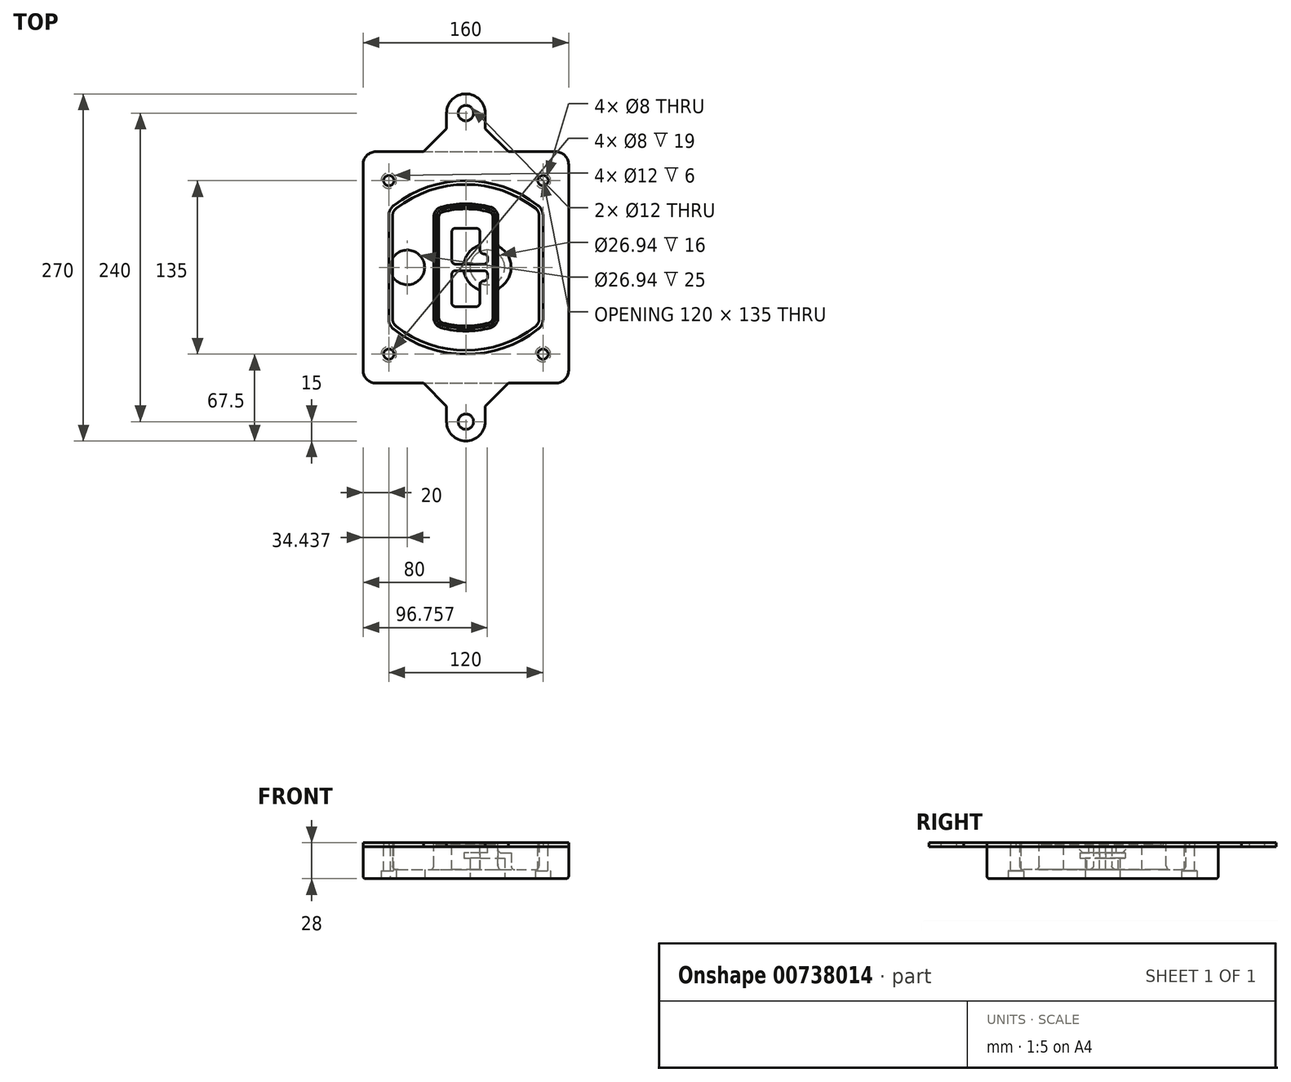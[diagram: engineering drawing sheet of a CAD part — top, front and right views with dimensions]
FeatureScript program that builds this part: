
annotation { "Feature Type Name" : "Feature", "Feature Type Description" : "" }
export const myFeature = defineFeature(function(context is Context, id is Id, definition is map)
    precondition{}
    {
        {
            var Q0;
            Q0=qCreatedBy(makeId("Top.planeOp"),FACE);
            var sketch = newSketch(context, id + "F0", { "sketchPlane" : qUnion([Q0])});
            skPoint(sketch, "E0.rect.middle", {"position": v(0, 0) * mm});
            skLineSegment(sketch, "E1.bottom", {"start": v(-70, -90) * mm, "end": v(70, -90) * mm});
            skLineSegment(sketch, "E1.top", {"start": v(-70, 90) * mm, "end": v(70, 90) * mm});
            skLineSegment(sketch, "E1.left", {"start": v(-80, -80) * mm, "end": v(-80, 80) * mm});
            skLineSegment(sketch, "E1.right", {"start": v(80, -80) * mm, "end": v(80, 80) * mm});
            skLineSegment(sketch, "E2", {"start": v(-80, 90) * mm, "end": v(80, -90) * mm, "construction": true});
            skLineSegment(sketch, "E3", {"start": v(80, 90) * mm, "end": v(-80, -90) * mm, "construction": true});
            skCircle(sketch, "E4", {"center": v(-60, 67.5) * mm, "radius": 4 * mm});
            skCircle(sketch, "E5", {"center": v(60, 67.5) * mm, "radius": 4 * mm});
            skCircle(sketch, "E6", {"center": v(60, -67.5) * mm, "radius": 4 * mm});
            skCircle(sketch, "E7", {"center": v(-60, -67.5) * mm, "radius": 4 * mm});
            skLineSegment(sketch, "E8", {"start": v(-60, 67.5) * mm, "end": v(60, 67.5) * mm, "construction": true});
            skLineSegment(sketch, "E9", {"start": v(60, 67.5) * mm, "end": v(60, -67.5) * mm, "construction": true});
            skLineSegment(sketch, "E10", {"start": v(60, -67.5) * mm, "end": v(-60, -67.5) * mm, "construction": true});
            skLineSegment(sketch, "E11", {"start": v(-60, -67.5) * mm, "end": v(-60, 67.5) * mm, "construction": true});
            skLineSegment(sketch, "E12", {"start": v(-60, 40.3) * mm, "end": v(-60, -40.3) * mm});
            skLineSegment(sketch, "E13", {"start": v(60, 40.3) * mm, "end": v(60, -40.3) * mm});
            skArc(sketch, "E14", {"start": v(56.15, 48.18) * mm, "mid": v(0, 67.5) * mm, "end": v(-56.15, 48.18) * mm});
            skArc(sketch, "E15", {"start": v(-56.15, -48.18) * mm, "mid": v(0, -67.5) * mm, "end": v(56.15, -48.18) * mm});
            skLineSegment(sketch, "E16", {"start": v(-60, 0) * mm, "end": v(60, 0) * mm, "construction": true});
            skPoint(sketch, "E17.visualSharp", {"position": v(-60, -45) * mm});
            skArc(sketch, "E17.filletArc", {"start": v(-60, -40.3) * mm, "mid": v(-58.99, -44.68) * mm, "end": v(-56.15, -48.18) * mm});
            skPoint(sketch, "E18.visualSharp", {"position": v(-60, 45) * mm});
            skArc(sketch, "E18.filletArc", {"start": v(-56.15, 48.18) * mm, "mid": v(-58.99, 44.68) * mm, "end": v(-60, 40.3) * mm});
            skPoint(sketch, "E19.visualSharp", {"position": v(60, 45) * mm});
            skArc(sketch, "E19.filletArc", {"start": v(60, 40.3) * mm, "mid": v(58.99, 44.68) * mm, "end": v(56.15, 48.18) * mm});
            skPoint(sketch, "E20.visualSharp", {"position": v(60, -45) * mm});
            skArc(sketch, "E20.filletArc", {"start": v(56.15, -48.18) * mm, "mid": v(58.99, -44.68) * mm, "end": v(60, -40.3) * mm});
            skPoint(sketch, "E21.visualSharp", {"position": v(-80, 90) * mm});
            skArc(sketch, "E21.filletArc", {"start": v(-70, 90) * mm, "mid": v(-77.07, 87.07) * mm, "end": v(-80, 80) * mm});
            skPoint(sketch, "E22.visualSharp", {"position": v(80, 90) * mm});
            skArc(sketch, "E22.filletArc", {"start": v(80, 80) * mm, "mid": v(77.07, 87.07) * mm, "end": v(70, 90) * mm});
            skPoint(sketch, "E23.visualSharp", {"position": v(80, -90) * mm});
            skArc(sketch, "E23.filletArc", {"start": v(70, -90) * mm, "mid": v(77.07, -87.07) * mm, "end": v(80, -80) * mm});
            skPoint(sketch, "E24.visualSharp", {"position": v(-80, -90) * mm});
            skArc(sketch, "E24.filletArc", {"start": v(-80, -80) * mm, "mid": v(-77.07, -87.07) * mm, "end": v(-70, -90) * mm});
            skArc(sketch, "E25.0", {"start": v(57, 40.3) * mm, "mid": v(56.3, 43.36) * mm, "end": v(54.3, 45.81) * mm});
            skLineSegment(sketch, "E25.1", {"start": v(57, 40.3) * mm, "end": v(57, -40.3) * mm});
            skArc(sketch, "E25.2", {"start": v(54.3, -45.81) * mm, "mid": v(56.3, -43.36) * mm, "end": v(57, -40.3) * mm});
            skArc(sketch, "E25.3", {"start": v(-54.3, -45.81) * mm, "mid": v(0, -64.5) * mm, "end": v(54.3, -45.81) * mm});
            skArc(sketch, "E25.4", {"start": v(-57, -40.3) * mm, "mid": v(-56.3, -43.36) * mm, "end": v(-54.3, -45.81) * mm});
            skArc(sketch, "E25.5", {"start": v(54.3, 45.81) * mm, "mid": v(0, 64.5) * mm, "end": v(-54.3, 45.81) * mm});
            skLineSegment(sketch, "E25.6", {"start": v(-57, 40.3) * mm, "end": v(-57, -40.3) * mm});
            skArc(sketch, "E25.7", {"start": v(-54.3, 45.81) * mm, "mid": v(-56.3, 43.36) * mm, "end": v(-57, 40.3) * mm});
            skArc(sketch, "E26.0", {"start": v(-58.62, 51.33) * mm, "mid": v(-62.58, 46.43) * mm, "end": v(-64, 40.3) * mm});
            skArc(sketch, "E26.1", {"start": v(58.62, 51.33) * mm, "mid": v(0, 71.5) * mm, "end": v(-58.62, 51.33) * mm});
            skArc(sketch, "E26.2", {"start": v(64, 40.3) * mm, "mid": v(62.58, 46.43) * mm, "end": v(58.62, 51.33) * mm});
            skLineSegment(sketch, "E26.3", {"start": v(64, 40.3) * mm, "end": v(64, -40.3) * mm});
            skArc(sketch, "E26.4", {"start": v(58.62, -51.33) * mm, "mid": v(62.58, -46.43) * mm, "end": v(64, -40.3) * mm});
            skLineSegment(sketch, "E26.5", {"start": v(-64, 40.3) * mm, "end": v(-64, -40.3) * mm});
            skArc(sketch, "E26.6", {"start": v(-58.62, -51.33) * mm, "mid": v(0, -71.5) * mm, "end": v(58.62, -51.33) * mm});
            skArc(sketch, "E26.7", {"start": v(-64, -40.3) * mm, "mid": v(-62.58, -46.43) * mm, "end": v(-58.62, -51.33) * mm});
            skSolve(sketch);
        }
        {
            var Q0;
            Q0=makeQuery(id+"F0.imprint","IMPRINT",FACE,{"disambiguationData":[TD([[makeQuery(id+"F0.imprint","IMPRINT",EDGE,{"derivedFrom":sQuery(id+"F0.wireOp",EDGE,"E1.bottom")}),1.0]])]});
            var Q1;
            Q1=makeQuery(id+"F0.imprint","IMPRINT",FACE,{"disambiguationData":[TD([[makeQuery(id+"F0.imprint","IMPRINT",EDGE,{"derivedFrom":sQuery(id+"F0.wireOp",EDGE,"E12")}),1.0]])]});
            var Q2;
            Q2=makeQuery(id+"F0.imprint","IMPRINT",FACE,{"disambiguationData":[TD([[makeQuery(id+"F0.imprint","IMPRINT",EDGE,{"derivedFrom":sQuery(id+"F0.wireOp",EDGE,"E25.0")}),1.0]])]});
            var Q3;
            Q3=makeQuery(id+"F0.imprint","IMPRINT",FACE,{"disambiguationData":[TD([[makeQuery(id+"F0.imprint","IMPRINT",EDGE,{"derivedFrom":sQuery(id+"F0.wireOp",EDGE,"E12")}),-1.0]])]});
            extrude(context, id + "F1", {"entities" : qUnion([Q0, Q1, Q2, Q3]), "oppositeDirection" : true, "depth" : 25 * mm});
        }
        {
            var Q0;
            Q0=makeQuery(id+"F0.imprint","IMPRINT",FACE,{"disambiguationData":[TD([[makeQuery(id+"F0.imprint","IMPRINT",EDGE,{"derivedFrom":sQuery(id+"F0.wireOp",EDGE,"E12")}),1.0]])]});
            extrude(context, id + "F2", {"entities" : qUnion([Q0]), "operationType" : NewBodyOperationType.ADD, "depth" : 3 * mm});
        }
        {
            var Q0;
            Q0=makeQuery(id+"F0.imprint","IMPRINT",FACE,{"disambiguationData":[TD([[makeQuery(id+"F0.imprint","IMPRINT",EDGE,{"derivedFrom":sQuery(id+"F0.wireOp",EDGE,"E25.0")}),1.0]])]});
            extrude(context, id + "F3", {"entities" : qUnion([Q0]), "operationType" : NewBodyOperationType.REMOVE, "oppositeDirection" : true, "depth" : 18 * mm});
        }
        {
            var Q0;
            Q0=makeQuery(id+"F2.opExtrude","CAP_FACE",FACE,{"disambiguationData":[OSD([sQuery(id+"F0.wireOp",EDGE,"E12"),sQuery(id+"F0.wireOp",EDGE,"E13"),sQuery(id+"F0.wireOp",EDGE,"E14"),sQuery(id+"F0.wireOp",EDGE,"E15"),sQuery(id+"F0.wireOp",EDGE,"E17.filletArc"),sQuery(id+"F0.wireOp",EDGE,"E18.filletArc"),sQuery(id+"F0.wireOp",EDGE,"E19.filletArc"),sQuery(id+"F0.wireOp",EDGE,"E20.filletArc"),sQuery(id+"F0.wireOp",EDGE,"E25.0"),sQuery(id+"F0.wireOp",EDGE,"E25.1"),sQuery(id+"F0.wireOp",EDGE,"E25.2"),sQuery(id+"F0.wireOp",EDGE,"E25.3"),sQuery(id+"F0.wireOp",EDGE,"E25.4"),sQuery(id+"F0.wireOp",EDGE,"E25.5"),sQuery(id+"F0.wireOp",EDGE,"E25.6"),sQuery(id+"F0.wireOp",EDGE,"E25.7")])],"isStart":false});
            var sketch = newSketch(context, id + "F4", { "sketchPlane" : qUnion([Q0])});
            skArc(sketch, "E27.0", {"start": v(-19.08, -46.97) * mm, "mid": v(0, -49.5) * mm, "end": v(19.08, -46.97) * mm});
            skArc(sketch, "E28.0", {"start": v(19.08, 46.97) * mm, "mid": v(0, 49.5) * mm, "end": v(-19.08, 46.97) * mm});
            skLineSegment(sketch, "E29", {"start": v(-25, 39.25) * mm, "end": v(-25, -39.25) * mm});
            skLineSegment(sketch, "E30", {"start": v(25, 39.25) * mm, "end": v(25, -39.25) * mm});
            skLineSegment(sketch, "E31", {"start": v(-25, 45.1) * mm, "end": v(25, 45.1) * mm, "construction": true});
            skLineSegment(sketch, "E32", {"start": v(-25, -45.1) * mm, "end": v(25, -45.1) * mm, "construction": true});
            skPoint(sketch, "E33.visualSharp", {"position": v(-25, 45.1) * mm});
            skArc(sketch, "E33.filletArc", {"start": v(-19.08, 46.97) * mm, "mid": v(-23.35, 44.11) * mm, "end": v(-25, 39.25) * mm});
            skPoint(sketch, "E34.visualSharp", {"position": v(25, 45.1) * mm});
            skArc(sketch, "E34.filletArc", {"start": v(25, 39.25) * mm, "mid": v(23.35, 44.11) * mm, "end": v(19.08, 46.97) * mm});
            skPoint(sketch, "E35.visualSharp", {"position": v(25, -45.1) * mm});
            skArc(sketch, "E35.filletArc", {"start": v(19.08, -46.97) * mm, "mid": v(23.35, -44.11) * mm, "end": v(25, -39.25) * mm});
            skPoint(sketch, "E36.visualSharp", {"position": v(-25, -45.1) * mm});
            skArc(sketch, "E36.filletArc", {"start": v(-25, -39.25) * mm, "mid": v(-23.35, -44.11) * mm, "end": v(-19.08, -46.97) * mm});
            skArc(sketch, "E37.0", {"start": v(54.3, 45.81) * mm, "mid": v(0, 64.5) * mm, "end": v(-54.3, 45.81) * mm});
            skArc(sketch, "E37.1", {"start": v(-54.3, 45.81) * mm, "mid": v(-56.3, 43.36) * mm, "end": v(-57, 40.3) * mm});
            skLineSegment(sketch, "E37.2", {"start": v(-57, 40.3) * mm, "end": v(-57, -40.3) * mm});
            skArc(sketch, "E37.3", {"start": v(-57, -40.3) * mm, "mid": v(-56.3, -43.36) * mm, "end": v(-54.3, -45.81) * mm});
            skArc(sketch, "E37.4", {"start": v(-54.3, -45.81) * mm, "mid": v(0, -64.5) * mm, "end": v(54.3, -45.81) * mm});
            skArc(sketch, "E37.5", {"start": v(54.3, -45.81) * mm, "mid": v(56.3, -43.36) * mm, "end": v(57, -40.3) * mm});
            skLineSegment(sketch, "E37.6", {"start": v(57, 40.3) * mm, "end": v(57, -40.3) * mm});
            skArc(sketch, "E37.7", {"start": v(57, 40.3) * mm, "mid": v(56.3, 43.36) * mm, "end": v(54.3, 45.81) * mm});
            skLineSegment(sketch, "E38.0", {"start": v(23, 39.25) * mm, "end": v(23, -39.25) * mm});
            skArc(sketch, "E38.1", {"start": v(18.56, -45.04) * mm, "mid": v(21.76, -42.9) * mm, "end": v(23, -39.25) * mm});
            skArc(sketch, "E38.2", {"start": v(-18.56, -45.04) * mm, "mid": v(0, -47.5) * mm, "end": v(18.56, -45.04) * mm});
            skArc(sketch, "E38.3", {"start": v(-23, -39.25) * mm, "mid": v(-21.76, -42.9) * mm, "end": v(-18.56, -45.04) * mm});
            skLineSegment(sketch, "E38.4", {"start": v(-23, 39.25) * mm, "end": v(-23, -39.25) * mm});
            skArc(sketch, "E38.5", {"start": v(23, 39.25) * mm, "mid": v(21.76, 42.9) * mm, "end": v(18.56, 45.04) * mm});
            skArc(sketch, "E38.6", {"start": v(-18.56, 45.04) * mm, "mid": v(-21.76, 42.9) * mm, "end": v(-23, 39.25) * mm});
            skArc(sketch, "E38.7", {"start": v(18.56, 45.04) * mm, "mid": v(0, 47.5) * mm, "end": v(-18.56, 45.04) * mm});
            skArc(sketch, "E39.0", {"start": v(21, 39.25) * mm, "mid": v(20.18, 41.68) * mm, "end": v(18.04, 43.1) * mm});
            skLineSegment(sketch, "E39.1", {"start": v(21, 39.25) * mm, "end": v(21, -39.25) * mm});
            skArc(sketch, "E39.2", {"start": v(18.04, -43.1) * mm, "mid": v(20.18, -41.68) * mm, "end": v(21, -39.25) * mm});
            skArc(sketch, "E39.3", {"start": v(-18.04, -43.1) * mm, "mid": v(0, -45.5) * mm, "end": v(18.04, -43.1) * mm});
            skArc(sketch, "E39.4", {"start": v(-21, -39.25) * mm, "mid": v(-20.18, -41.68) * mm, "end": v(-18.04, -43.1) * mm});
            skArc(sketch, "E39.5", {"start": v(18.04, 43.1) * mm, "mid": v(0, 45.5) * mm, "end": v(-18.04, 43.1) * mm});
            skLineSegment(sketch, "E39.6", {"start": v(-21, 39.25) * mm, "end": v(-21, -39.25) * mm});
            skArc(sketch, "E39.7", {"start": v(-18.04, 43.1) * mm, "mid": v(-20.18, 41.68) * mm, "end": v(-21, 39.25) * mm});
            skLineSegment(sketch, "E40", {"start": v(-25, 0) * mm, "end": v(25, 0) * mm, "construction": true});
            skLineSegment(sketch, "E41", {"start": v(-11, 5.5) * mm, "end": v(-11, 27.5) * mm});
            skLineSegment(sketch, "E42", {"start": v(-8, 30.5) * mm, "end": v(8, 30.5) * mm});
            skLineSegment(sketch, "E43", {"start": v(11, 27.5) * mm, "end": v(11, 13.5) * mm});
            skLineSegment(sketch, "E44", {"start": v(14, 10.5) * mm, "end": v(14, 10.5) * mm});
            skLineSegment(sketch, "E45", {"start": v(17, 7.5) * mm, "end": v(17, 5.5) * mm});
            skLineSegment(sketch, "E46", {"start": v(14, 2.5) * mm, "end": v(-8, 2.5) * mm});
            skPoint(sketch, "E47.visualSharp", {"position": v(-11, 30.5) * mm});
            skArc(sketch, "E47.filletArc", {"start": v(-8, 30.5) * mm, "mid": v(-10.12, 29.62) * mm, "end": v(-11, 27.5) * mm});
            skPoint(sketch, "E48.visualSharp", {"position": v(11, 30.5) * mm});
            skArc(sketch, "E48.filletArc", {"start": v(11, 27.5) * mm, "mid": v(10.12, 29.62) * mm, "end": v(8, 30.5) * mm});
            skPoint(sketch, "E49.visualSharp", {"position": v(11, 10.5) * mm});
            skArc(sketch, "E49.filletArc", {"start": v(11, 13.5) * mm, "mid": v(11.88, 11.38) * mm, "end": v(14, 10.5) * mm});
            skPoint(sketch, "E50.visualSharp", {"position": v(17, 10.5) * mm});
            skArc(sketch, "E50.filletArc", {"start": v(17, 7.5) * mm, "mid": v(16.12, 9.62) * mm, "end": v(14, 10.5) * mm});
            skPoint(sketch, "E51.visualSharp", {"position": v(17, 2.5) * mm});
            skArc(sketch, "E51.filletArc", {"start": v(14, 2.5) * mm, "mid": v(16.12, 3.38) * mm, "end": v(17, 5.5) * mm});
            skPoint(sketch, "E52.visualSharp", {"position": v(-11, 2.5) * mm});
            skArc(sketch, "E52.filletArc", {"start": v(-11, 5.5) * mm, "mid": v(-10.12, 3.38) * mm, "end": v(-8, 2.5) * mm});
            skLineSegment(sketch, "E53.0.MirrorCS", {"start": v(14, -2.5) * mm, "end": v(-8, -2.5) * mm});
            skArc(sketch, "E54.0.MirrorCS", {"start": v(-11, -5.5) * mm, "mid": v(-10.12, -3.38) * mm, "end": v(-8, -2.5) * mm});
            skLineSegment(sketch, "E55.0.MirrorCS", {"start": v(-11, -5.5) * mm, "end": v(-11, -27.5) * mm});
            skArc(sketch, "E56.0.MirrorCS", {"start": v(-8, -30.5) * mm, "mid": v(-10.12, -29.62) * mm, "end": v(-11, -27.5) * mm});
            skLineSegment(sketch, "E57.0.MirrorCS", {"start": v(-8, -30.5) * mm, "end": v(8, -30.5) * mm});
            skArc(sketch, "E58.0.MirrorCS", {"start": v(11, -27.5) * mm, "mid": v(10.12, -29.62) * mm, "end": v(8, -30.5) * mm});
            skLineSegment(sketch, "E59.0.MirrorCS", {"start": v(11, -27.5) * mm, "end": v(11, -13.5) * mm});
            skArc(sketch, "E60.0.MirrorCS", {"start": v(11, -13.5) * mm, "mid": v(11.88, -11.38) * mm, "end": v(14, -10.5) * mm});
            skArc(sketch, "E61.0.MirrorCS", {"start": v(17, -7.5) * mm, "mid": v(16.12, -9.62) * mm, "end": v(14, -10.5) * mm});
            skLineSegment(sketch, "E62.0.MirrorCS", {"start": v(17, -7.5) * mm, "end": v(17, -5.5) * mm});
            skArc(sketch, "E63.0.MirrorCS", {"start": v(14, -2.5) * mm, "mid": v(16.12, -3.38) * mm, "end": v(17, -5.5) * mm});
            skSolve(sketch);
        }
        {
            var Q0;
            Q0=makeQuery(id+"F4.imprint","IMPRINT",FACE,{"disambiguationData":[TD([[makeQuery(id+"F4.imprint","IMPRINT",EDGE,{"derivedFrom":sQuery(id+"F4.wireOp",EDGE,"E27.0")}),1.0]])]});
            var Q1;
            Q1=makeQuery(id+"F4.imprint","IMPRINT",FACE,{"disambiguationData":[TD([[makeQuery(id+"F4.imprint","IMPRINT",EDGE,{"derivedFrom":sQuery(id+"F4.wireOp",EDGE,"E38.0")}),-1.0]])]});
            var Q2;
            Q2=makeQuery(id+"F4.imprint","IMPRINT",FACE,{"disambiguationData":[TD([[makeQuery(id+"F4.imprint","IMPRINT",EDGE,{"derivedFrom":sQuery(id+"F4.wireOp",EDGE,"E39.0")}),1.0]])]});
            extrude(context, id + "F5", {"entities" : qUnion([Q0, Q1, Q2]), "operationType" : NewBodyOperationType.ADD, "endBound" : BoundingType.UP_TO_NEXT, "oppositeDirection" : true, "depth" : 25 * mm});
        }
        {
            var Q0;
            Q0=makeQuery(id+"F4.imprint","IMPRINT",FACE,{"disambiguationData":[TD([[makeQuery(id+"F4.imprint","IMPRINT",EDGE,{"derivedFrom":sQuery(id+"F4.wireOp",EDGE,"E38.0")}),-1.0]])]});
            extrude(context, id + "F6", {"entities" : qUnion([Q0]), "operationType" : NewBodyOperationType.REMOVE, "oppositeDirection" : true, "depth" : 2 * mm});
        }
        {
            var Q0;
            Q0=makeQuery(id+"F1.opExtrude","CAP_FACE",FACE,{"disambiguationData":[OSD([sQuery(id+"F0.wireOp",EDGE,"E1.bottom"),sQuery(id+"F0.wireOp",EDGE,"E1.top"),sQuery(id+"F0.wireOp",EDGE,"E1.left"),sQuery(id+"F0.wireOp",EDGE,"E1.right"),sQuery(id+"F0.wireOp",EDGE,"E4"),sQuery(id+"F0.wireOp",EDGE,"E5"),sQuery(id+"F0.wireOp",EDGE,"E6"),sQuery(id+"F0.wireOp",EDGE,"E7"),sQuery(id+"F0.wireOp",EDGE,"E21.filletArc"),sQuery(id+"F0.wireOp",EDGE,"E22.filletArc"),sQuery(id+"F0.wireOp",EDGE,"E23.filletArc"),sQuery(id+"F0.wireOp",EDGE,"E24.filletArc")])],"isStart":false});
            var sketch = newSketch(context, id + "F7", { "sketchPlane" : qUnion([Q0])});
            skCircle(sketch, "E64", {"center": v(16.76, 0) * mm, "radius": 13.47 * mm});
            skCircle(sketch, "E65", {"center": v(-45.56, 0) * mm, "radius": 13.47 * mm});
            skLineSegment(sketch, "E66", {"start": v(80, 0) * mm, "end": v(-80, 0) * mm});
            skCircle(sketch, "E67", {"center": v(16.76, 0) * mm, "radius": 18.47 * mm});
            skCircle(sketch, "E68", {"center": v(60, -67.5) * mm, "radius": 6 * mm});
            skCircle(sketch, "E69", {"center": v(-60, -67.5) * mm, "radius": 6 * mm});
            skCircle(sketch, "E70", {"center": v(-60, 67.5) * mm, "radius": 6 * mm});
            skCircle(sketch, "E71", {"center": v(60, 67.5) * mm, "radius": 6 * mm});
            skSolve(sketch);
        }
        {
            var Q0;
            {var subQ1=sQuery(id+"F7.wireOp",EDGE,"E66");var subQ4=sQuery(id+"F7.wireOp",EDGE,"E64");var subQ6=makeQuery(id+"F7.imprint","INTERSECT",VERTEX,{"disambiguationData":[OD(0.0)],"derivedFrom":[subQ4,subQ1]});Q0=makeQuery(id+"F7.imprint","IMPRINT",FACE,{"disambiguationData":[TD([[makeQuery(id+"F7.imprint","IMPRINT",EDGE,{"disambiguationData":[TD([[subQ6,-1.0]])],"derivedFrom":subQ4}),-1.0]])]});}
            var Q1;
            {var subQ0=sQuery(id+"F7.wireOp",EDGE,"E66");var subQ1=sQuery(id+"F7.wireOp",EDGE,"E64");var subQ3=makeQuery(id+"F7.imprint","INTERSECT",VERTEX,{"disambiguationData":[OD(0.0)],"derivedFrom":[subQ1,subQ0]});Q1=makeQuery(id+"F7.imprint","IMPRINT",FACE,{"disambiguationData":[TD([[makeQuery(id+"F7.imprint","IMPRINT",EDGE,{"disambiguationData":[TD([[subQ3,-1.0]])],"derivedFrom":subQ1}),1.0]])]});}
            var Q2;
            {var subQ0=sQuery(id+"F7.wireOp",EDGE,"E66");var subQ1=sQuery(id+"F7.wireOp",EDGE,"E64");var subQ3=makeQuery(id+"F7.imprint","INTERSECT",VERTEX,{"disambiguationData":[OD(0.0)],"derivedFrom":[subQ1,subQ0]});Q2=makeQuery(id+"F7.imprint","IMPRINT",FACE,{"disambiguationData":[TD([[makeQuery(id+"F7.imprint","IMPRINT",EDGE,{"disambiguationData":[TD([[subQ3,1.0]])],"derivedFrom":subQ1}),1.0]])]});}
            var Q3;
            {var subQ1=sQuery(id+"F7.wireOp",EDGE,"E66");var subQ4=sQuery(id+"F7.wireOp",EDGE,"E64");var subQ6=makeQuery(id+"F7.imprint","INTERSECT",VERTEX,{"disambiguationData":[OD(0.0)],"derivedFrom":[subQ4,subQ1]});Q3=makeQuery(id+"F7.imprint","IMPRINT",FACE,{"disambiguationData":[TD([[makeQuery(id+"F7.imprint","IMPRINT",EDGE,{"disambiguationData":[TD([[subQ6,1.0]])],"derivedFrom":subQ4}),-1.0]])]});}
            extrude(context, id + "F8", {"entities" : qUnion([Q0, Q1, Q2, Q3]), "operationType" : NewBodyOperationType.ADD, "oppositeDirection" : true, "depth" : 20 * mm});
        }
        {
            var Q0;
            {var subQ0=sQuery(id+"F7.wireOp",EDGE,"E66");var subQ1=sQuery(id+"F7.wireOp",EDGE,"E64");var subQ3=makeQuery(id+"F7.imprint","INTERSECT",VERTEX,{"disambiguationData":[OD(0.0)],"derivedFrom":[subQ1,subQ0]});Q0=makeQuery(id+"F7.imprint","IMPRINT",FACE,{"disambiguationData":[TD([[makeQuery(id+"F7.imprint","IMPRINT",EDGE,{"disambiguationData":[TD([[subQ3,-1.0]])],"derivedFrom":subQ1}),1.0]])]});}
            var Q1;
            {var subQ0=sQuery(id+"F7.wireOp",EDGE,"E66");var subQ1=sQuery(id+"F7.wireOp",EDGE,"E64");var subQ3=makeQuery(id+"F7.imprint","INTERSECT",VERTEX,{"disambiguationData":[OD(0.0)],"derivedFrom":[subQ1,subQ0]});Q1=makeQuery(id+"F7.imprint","IMPRINT",FACE,{"disambiguationData":[TD([[makeQuery(id+"F7.imprint","IMPRINT",EDGE,{"disambiguationData":[TD([[subQ3,1.0]])],"derivedFrom":subQ1}),1.0]])]});}
            extrude(context, id + "F9", {"entities" : qUnion([Q0, Q1]), "operationType" : NewBodyOperationType.REMOVE, "oppositeDirection" : true, "depth" : 16 * mm});
        }
        {
            var Q0;
            {var subQ0=sQuery(id+"F7.wireOp",EDGE,"E66");var subQ1=sQuery(id+"F7.wireOp",EDGE,"E65");var subQ3=makeQuery(id+"F7.imprint","INTERSECT",VERTEX,{"disambiguationData":[OD(0.0)],"derivedFrom":[subQ1,subQ0]});Q0=makeQuery(id+"F7.imprint","IMPRINT",FACE,{"disambiguationData":[TD([[makeQuery(id+"F7.imprint","IMPRINT",EDGE,{"disambiguationData":[TD([[subQ3,-1.0]])],"derivedFrom":subQ1}),1.0]])]});}
            var Q1;
            {var subQ0=sQuery(id+"F7.wireOp",EDGE,"E66");var subQ1=sQuery(id+"F7.wireOp",EDGE,"E65");var subQ3=makeQuery(id+"F7.imprint","INTERSECT",VERTEX,{"disambiguationData":[OD(0.0)],"derivedFrom":[subQ1,subQ0]});Q1=makeQuery(id+"F7.imprint","IMPRINT",FACE,{"disambiguationData":[TD([[makeQuery(id+"F7.imprint","IMPRINT",EDGE,{"disambiguationData":[TD([[subQ3,1.0]])],"derivedFrom":subQ1}),1.0]])]});}
            extrude(context, id + "F10", {"entities" : qUnion([Q0, Q1]), "operationType" : NewBodyOperationType.REMOVE, "oppositeDirection" : true, "depth" : 25 * mm});
        }
        {
            var Q0;
            Q0=makeQuery(id+"F7.imprint","IMPRINT",FACE,{"disambiguationData":[TD([[makeQuery(id+"F7.imprint","IMPRINT",EDGE,{"derivedFrom":sQuery(id+"F7.wireOp",EDGE,"E68")}),1.0]])]});
            var Q1;
            Q1=makeQuery(id+"F7.imprint","IMPRINT",FACE,{"disambiguationData":[TD([[makeQuery(id+"F7.imprint","IMPRINT",EDGE,{"derivedFrom":makeQuery(id+"F1.opExtrude","CAP_EDGE",EDGE,{"disambiguationData":[OSD([sQuery(id+"F0.wireOp",EDGE,"E5")])],"isStart":false})}),-1.0]])]});
            var Q2;
            Q2=makeQuery(id+"F7.imprint","IMPRINT",FACE,{"disambiguationData":[TD([[makeQuery(id+"F7.imprint","IMPRINT",EDGE,{"derivedFrom":sQuery(id+"F7.wireOp",EDGE,"E69")}),1.0]])]});
            var Q3;
            Q3=makeQuery(id+"F7.imprint","IMPRINT",FACE,{"disambiguationData":[TD([[makeQuery(id+"F7.imprint","IMPRINT",EDGE,{"derivedFrom":makeQuery(id+"F1.opExtrude","CAP_EDGE",EDGE,{"disambiguationData":[OSD([sQuery(id+"F0.wireOp",EDGE,"E4")])],"isStart":false})}),-1.0]])]});
            var Q4;
            Q4=makeQuery(id+"F7.imprint","IMPRINT",FACE,{"disambiguationData":[TD([[makeQuery(id+"F7.imprint","IMPRINT",EDGE,{"derivedFrom":sQuery(id+"F7.wireOp",EDGE,"E70")}),1.0]])]});
            var Q5;
            Q5=makeQuery(id+"F7.imprint","IMPRINT",FACE,{"disambiguationData":[TD([[makeQuery(id+"F7.imprint","IMPRINT",EDGE,{"derivedFrom":makeQuery(id+"F1.opExtrude","CAP_EDGE",EDGE,{"disambiguationData":[OSD([sQuery(id+"F0.wireOp",EDGE,"E7")])],"isStart":false})}),-1.0]])]});
            var Q6;
            Q6=makeQuery(id+"F7.imprint","IMPRINT",FACE,{"disambiguationData":[TD([[makeQuery(id+"F7.imprint","IMPRINT",EDGE,{"derivedFrom":sQuery(id+"F7.wireOp",EDGE,"E71")}),1.0]])]});
            var Q7;
            Q7=makeQuery(id+"F7.imprint","IMPRINT",FACE,{"disambiguationData":[TD([[makeQuery(id+"F7.imprint","IMPRINT",EDGE,{"derivedFrom":makeQuery(id+"F1.opExtrude","CAP_EDGE",EDGE,{"disambiguationData":[OSD([sQuery(id+"F0.wireOp",EDGE,"E6")])],"isStart":false})}),-1.0]])]});
            extrude(context, id + "F11", {"entities" : qUnion([Q0, Q1, Q2, Q3, Q4, Q5, Q6, Q7]), "operationType" : NewBodyOperationType.REMOVE, "oppositeDirection" : true, "depth" : 6 * mm});
        }
        {
            var Q0;
            Q0=makeQuery(id+"F9.boolean.opBoolean","COPY",FACE,{"derivedFrom":makeQuery(id+"F9.opExtrude","CAP_FACE",FACE,{"disambiguationData":[OSD([sQuery(id+"F7.wireOp",EDGE,"E64")])],"isStart":false})});
            var sketch = newSketch(context, id + "F12", { "sketchPlane" : qUnion([Q0])});
            skArc(sketch, "E72.0", {"start": v(11, 17.55) * mm, "mid": v(2.57, 11.82) * mm, "end": v(-1.54, 2.5) * mm});
            skArc(sketch, "E72.1", {"start": v(-1.54, -2.5) * mm, "mid": v(2.57, -11.82) * mm, "end": v(11, -17.55) * mm});
            skLineSegment(sketch, "E73", {"start": v(-1.54, -2.5) * mm, "end": v(14, -2.5) * mm});
            skLineSegment(sketch, "E74.0", {"start": v(14, 2.5) * mm, "end": v(-1.54, 2.5) * mm});
            skArc(sketch, "E74.1", {"start": v(14, 2.5) * mm, "mid": v(16.12, 3.38) * mm, "end": v(17, 5.5) * mm});
            skLineSegment(sketch, "E74.2", {"start": v(17, 7.5) * mm, "end": v(17, 5.5) * mm});
            skArc(sketch, "E74.3", {"start": v(17, 7.5) * mm, "mid": v(16.12, 9.62) * mm, "end": v(14, 10.5) * mm});
            skArc(sketch, "E74.4", {"start": v(11, 13.5) * mm, "mid": v(11.88, 11.38) * mm, "end": v(14, 10.5) * mm});
            skLineSegment(sketch, "E74.5", {"start": v(11, 17.55) * mm, "end": v(11, 13.5) * mm});
            skLineSegment(sketch, "E74.7", {"start": v(14, -2.5) * mm, "end": v(-1.54, -2.5) * mm});
            skArc(sketch, "E74.8", {"start": v(14, -2.5) * mm, "mid": v(16.12, -3.38) * mm, "end": v(17, -5.5) * mm});
            skLineSegment(sketch, "E74.9", {"start": v(17, -7.5) * mm, "end": v(17, -5.5) * mm});
            skArc(sketch, "E74.10", {"start": v(17, -7.5) * mm, "mid": v(16.12, -9.62) * mm, "end": v(14, -10.5) * mm});
            skArc(sketch, "E74.11", {"start": v(11, -13.5) * mm, "mid": v(11.88, -11.38) * mm, "end": v(14, -10.5) * mm});
            skLineSegment(sketch, "E74.12", {"start": v(11, -17.55) * mm, "end": v(11, -13.5) * mm});
            skPoint(sketch, "E75.orphan", {"position": v(11, -27.5) * mm});
            skPoint(sketch, "E76.orphan", {"position": v(-8, -2.5) * mm});
            skPoint(sketch, "E77.orphan", {"position": v(-8, 2.5) * mm});
            skPoint(sketch, "E78.orphan", {"position": v(11, 27.5) * mm});
            skSolve(sketch);
        }
        {
            var Q0;
            {var subQ7=sQuery(id+"F12.wireOp",EDGE,"E72.0");var subQ14=sQuery(id+"F12.wireOp",EDGE,"E72.1");var subQ16=sQuery(id+"F12.wireOp",EDGE,"E74.1");var subQ18=sQuery(id+"F12.wireOp",EDGE,"E74.8");Q0=qUnion([makeQuery(id+"F12.imprint","IMPRINT",FACE,{"disambiguationData":[TD([[makeQuery(id+"F12.imprint","IMPRINT",EDGE,{"derivedFrom":subQ7}),1.0]])]}),makeQuery(id+"F12.imprint","IMPRINT",FACE,{"disambiguationData":[TD([[makeQuery(id+"F12.imprint","IMPRINT",EDGE,{"derivedFrom":subQ14}),1.0]])]}),makeQuery(id+"F12.imprint","IMPRINT",FACE,{"disambiguationData":[TD([[makeQuery(id+"F12.imprint","IMPRINT",EDGE,{"derivedFrom":subQ16}),1.0]])]}),makeQuery(id+"F12.imprint","IMPRINT",FACE,{"disambiguationData":[TD([[makeQuery(id+"F12.imprint","IMPRINT",EDGE,{"derivedFrom":subQ18}),-1.0]])]})]);}
            var Q1;
            Q1=makeQuery(id+"F5.boolean.opBoolean","SPLIT",FACE,{"disambiguationData":[TD([makeQuery(id+"F5.opExtrude","SWEPT_FACE",FACE,{"disambiguationData":[OSD([sQuery(id+"F4.wireOp",EDGE,"E41")])]})])],"derivedFrom":makeQuery(id+"F3.boolean.opBoolean","COPY",FACE,{"derivedFrom":makeQuery(id+"F3.opExtrude","CAP_FACE",FACE,{"disambiguationData":[OSD([sQuery(id+"F0.wireOp",EDGE,"E25.0"),sQuery(id+"F0.wireOp",EDGE,"E25.1"),sQuery(id+"F0.wireOp",EDGE,"E25.2"),sQuery(id+"F0.wireOp",EDGE,"E25.3"),sQuery(id+"F0.wireOp",EDGE,"E25.4"),sQuery(id+"F0.wireOp",EDGE,"E25.5"),sQuery(id+"F0.wireOp",EDGE,"E25.6"),sQuery(id+"F0.wireOp",EDGE,"E25.7")])],"isStart":false})})});
            extrude(context, id + "F13", {"entities" : qUnion([Q0]), "operationType" : NewBodyOperationType.REMOVE, "endBound" : BoundingType.UP_TO_SURFACE, "endBoundEntityFace" : qUnion([Q1]), "depth" : 25 * mm});
        }
        {
            var Q0;
            Q0=makeQuery(id+"F3.boolean.opBoolean","COPY",EDGE,{"derivedFrom":makeQuery(id+"F3.opExtrude","CAP_EDGE",EDGE,{"disambiguationData":[OSD([sQuery(id+"F0.wireOp",EDGE,"E25.6")])],"isStart":false})});
            var Q1;
            Q1=makeQuery(id+"F8.boolean.opBoolean","INTERSECT",EDGE,{"derivedFrom":[makeQuery(id+"F5.opExtrude","SWEPT_FACE",FACE,{"disambiguationData":[OSD([sQuery(id+"F4.wireOp",EDGE,"E30")])]}),makeQuery(id+"F8.opExtrude","CAP_FACE",FACE,{"disambiguationData":[OSD([sQuery(id+"F7.wireOp",EDGE,"E67")])],"isStart":false})]});
            var Q2;
            Q2=makeQuery(id+"F8.boolean.opBoolean","INTERSECT",EDGE,{"disambiguationData":[OD(1.0)],"derivedFrom":[makeQuery(id+"F5.opExtrude","SWEPT_FACE",FACE,{"disambiguationData":[OSD([sQuery(id+"F4.wireOp",EDGE,"E30")])]}),makeQuery(id+"F8.opExtrude","SWEPT_FACE",FACE,{"disambiguationData":[OSD([sQuery(id+"F7.wireOp",EDGE,"E67")])]})]});
            var Q3;
            {var subQ0=sQuery(id+"F4.wireOp",EDGE,"E30");Q3=makeQuery(id+"F8.boolean.opBoolean","SPLIT",EDGE,{"disambiguationData":[TD([makeQuery(id+"F5.opExtrude","SWEPT_FACE",FACE,{"disambiguationData":[OSD([sQuery(id+"F4.wireOp",EDGE,"E35.filletArc")])]})])],"derivedFrom":makeQuery(id+"F5.opExtrude","CAP_EDGE",EDGE,{"disambiguationData":[OSD([subQ0])],"isStart":false})});}
            var Q4;
            {var subQ0=sQuery(id+"F0.wireOp",EDGE,"E25.7");var subQ1=sQuery(id+"F0.wireOp",EDGE,"E25.1");var subQ2=sQuery(id+"F0.wireOp",EDGE,"E25.6");var subQ3=sQuery(id+"F0.wireOp",EDGE,"E25.5");var subQ4=sQuery(id+"F0.wireOp",EDGE,"E25.4");var subQ5=sQuery(id+"F0.wireOp",EDGE,"E25.0");var subQ6=sQuery(id+"F0.wireOp",EDGE,"E25.2");var subQ7=sQuery(id+"F0.wireOp",EDGE,"E25.3");Q4=makeQuery(id+"F8.boolean.opBoolean","INTERSECT",EDGE,{"derivedFrom":[makeQuery(id+"F5.boolean.opBoolean","SPLIT",FACE,{"disambiguationData":[TD([makeQuery(id+"F2.opExtrude","SWEPT_FACE",FACE,{"disambiguationData":[OSD([subQ5])]})])],"derivedFrom":makeQuery(id+"F3.boolean.opBoolean","COPY",FACE,{"derivedFrom":makeQuery(id+"F3.opExtrude","CAP_FACE",FACE,{"disambiguationData":[OSD([subQ5,subQ1,subQ6,subQ7,subQ4,subQ3,subQ2,subQ0])],"isStart":false})})}),makeQuery(id+"F8.opExtrude","SWEPT_FACE",FACE,{"disambiguationData":[OSD([sQuery(id+"F7.wireOp",EDGE,"E67")])]})]});}
            var Q5;
            Q5=makeQuery(id+"F8.boolean.opBoolean","INTERSECT",EDGE,{"disambiguationData":[OD(0.0)],"derivedFrom":[makeQuery(id+"F5.opExtrude","SWEPT_FACE",FACE,{"disambiguationData":[OSD([sQuery(id+"F4.wireOp",EDGE,"E30")])]}),makeQuery(id+"F8.opExtrude","SWEPT_FACE",FACE,{"disambiguationData":[OSD([sQuery(id+"F7.wireOp",EDGE,"E67")])]})]});
            fillet(context, id + "F14", {"entities" : qUnion([Q0, Q1, Q2, Q3, Q4, Q5]), "radius" : 3 * mm, "tangentPropagation" : true, "allowEdgeOverflow" : false});
        }
        {
            var Q0;
            Q0=makeQuery(id+"F1.opExtrude","CAP_EDGE",EDGE,{"disambiguationData":[OSD([sQuery(id+"F0.wireOp",EDGE,"E1.bottom")])],"isStart":false});
            fillet(context, id + "F15", {"entities" : qUnion([Q0]), "radius" : 2 * mm, "tangentPropagation" : true, "allowEdgeOverflow" : false});
        }
        {
            var Q0;
            {var subQ0=sQuery(id+"F0.wireOp",EDGE,"E21.filletArc");var subQ1=sQuery(id+"F0.wireOp",EDGE,"E7");var subQ2=sQuery(id+"F0.wireOp",EDGE,"E6");var subQ3=sQuery(id+"F0.wireOp",EDGE,"E5");var subQ4=sQuery(id+"F0.wireOp",EDGE,"E4");var subQ5=sQuery(id+"F0.wireOp",EDGE,"E22.filletArc");var subQ6=sQuery(id+"F0.wireOp",EDGE,"E1.bottom");var subQ7=sQuery(id+"F0.wireOp",EDGE,"E1.right");var subQ8=sQuery(id+"F0.wireOp",EDGE,"E1.top");var subQ9=sQuery(id+"F0.wireOp",EDGE,"E1.left");var subQ10=sQuery(id+"F0.wireOp",EDGE,"E23.filletArc");var subQ11=sQuery(id+"F0.wireOp",EDGE,"E24.filletArc");Q0=makeQuery(id+"F2.boolean.opBoolean","SPLIT",FACE,{"disambiguationData":[TD([makeQuery(id+"F1.opExtrude","SWEPT_FACE",FACE,{"disambiguationData":[OSD([subQ6])]})])],"derivedFrom":makeQuery(id+"F1.opExtrude","CAP_FACE",FACE,{"disambiguationData":[OSD([subQ6,subQ8,subQ9,subQ7,subQ4,subQ3,subQ2,subQ1,subQ0,subQ5,subQ10,subQ11])],"isStart":true})});}
            var sketch = newSketch(context, id + "F16", { "sketchPlane" : qUnion([Q0])});
            skLineSegment(sketch, "E79", {"start": v(0, 90) * mm, "end": v(0, 120) * mm, "construction": true});
            skCircle(sketch, "E80", {"center": v(0, 120) * mm, "radius": 6 * mm});
            skLineSegment(sketch, "E81", {"start": v(-33, 90) * mm, "end": v(-15, 108) * mm});
            skLineSegment(sketch, "E82", {"start": v(-15, 108) * mm, "end": v(-15, 120) * mm});
            skLineSegment(sketch, "E83", {"start": v(33, 90) * mm, "end": v(15, 108) * mm});
            skLineSegment(sketch, "E84", {"start": v(15, 108) * mm, "end": v(15, 120) * mm});
            skArc(sketch, "E85", {"start": v(15, 120) * mm, "mid": v(0, 135) * mm, "end": v(-15, 120) * mm});
            skLineSegment(sketch, "E86", {"start": v(-80, 0) * mm, "end": v(80, 0) * mm, "construction": true});
            skLineSegment(sketch, "E87.MirrorCS", {"start": v(33, -90) * mm, "end": v(15, -108) * mm});
            skLineSegment(sketch, "E88.MirrorCS", {"start": v(15, -108) * mm, "end": v(15, -120) * mm});
            skArc(sketch, "E89.MirrorCS", {"start": v(15, -120) * mm, "mid": v(0, -135) * mm, "end": v(-15, -120) * mm});
            skLineSegment(sketch, "E90.MirrorCS", {"start": v(-15, -108) * mm, "end": v(-15, -120) * mm});
            skLineSegment(sketch, "E91.MirrorCS", {"start": v(-33, -90) * mm, "end": v(-15, -108) * mm});
            skLineSegment(sketch, "E92.MirrorCS", {"start": v(0, -90) * mm, "end": v(0, -120) * mm, "construction": true});
            skCircle(sketch, "E93.MirrorC", {"center": v(0, -120) * mm, "radius": 6 * mm});
            skSolve(sketch);
        }
        {
            var Q0;
            Q0=makeQuery(id+"F16.imprint","IMPRINT",FACE,{"disambiguationData":[TD([[makeQuery(id+"F16.imprint","IMPRINT",EDGE,{"derivedFrom":sQuery(id+"F16.wireOp",EDGE,"E80")}),-1.0]])]});
            var Q1;
            Q1=makeQuery(id+"F16.imprint","IMPRINT",FACE,{"disambiguationData":[TD([[makeQuery(id+"F16.imprint","IMPRINT",EDGE,{"derivedFrom":makeQuery(id+"F1.opExtrude","CAP_EDGE",EDGE,{"disambiguationData":[OSD([sQuery(id+"F0.wireOp",EDGE,"E1.left")])],"isStart":true})}),-1.0]])]});
            var Q2;
            {var subQ0=sQuery(id+"F16.wireOp",EDGE,"E87.MirrorCS");Q2=makeQuery(id+"F16.imprint","IMPRINT",FACE,{"disambiguationData":[TD([[makeQuery(id+"F16.imprint","IMPRINT",EDGE,{"derivedFrom":subQ0}),-1.0]])]});}
            var Q3;
            Q3=makeQuery(id+"F2.opExtrude","CAP_FACE",FACE,{"disambiguationData":[OSD([sQuery(id+"F0.wireOp",EDGE,"E12"),sQuery(id+"F0.wireOp",EDGE,"E13"),sQuery(id+"F0.wireOp",EDGE,"E14"),sQuery(id+"F0.wireOp",EDGE,"E15"),sQuery(id+"F0.wireOp",EDGE,"E17.filletArc"),sQuery(id+"F0.wireOp",EDGE,"E18.filletArc"),sQuery(id+"F0.wireOp",EDGE,"E19.filletArc"),sQuery(id+"F0.wireOp",EDGE,"E20.filletArc"),sQuery(id+"F0.wireOp",EDGE,"E25.0"),sQuery(id+"F0.wireOp",EDGE,"E25.1"),sQuery(id+"F0.wireOp",EDGE,"E25.2"),sQuery(id+"F0.wireOp",EDGE,"E25.3"),sQuery(id+"F0.wireOp",EDGE,"E25.4"),sQuery(id+"F0.wireOp",EDGE,"E25.5"),sQuery(id+"F0.wireOp",EDGE,"E25.6"),sQuery(id+"F0.wireOp",EDGE,"E25.7")])],"isStart":false});
            extrude(context, id + "F17", {"entities" : qUnion([Q0, Q1, Q2]), "endBound" : BoundingType.UP_TO_SURFACE, "depth" : 25 * mm, "endBoundEntityFace" : qUnion([Q3]), "offsetDistance" : 25 * mm});
        }
    });
